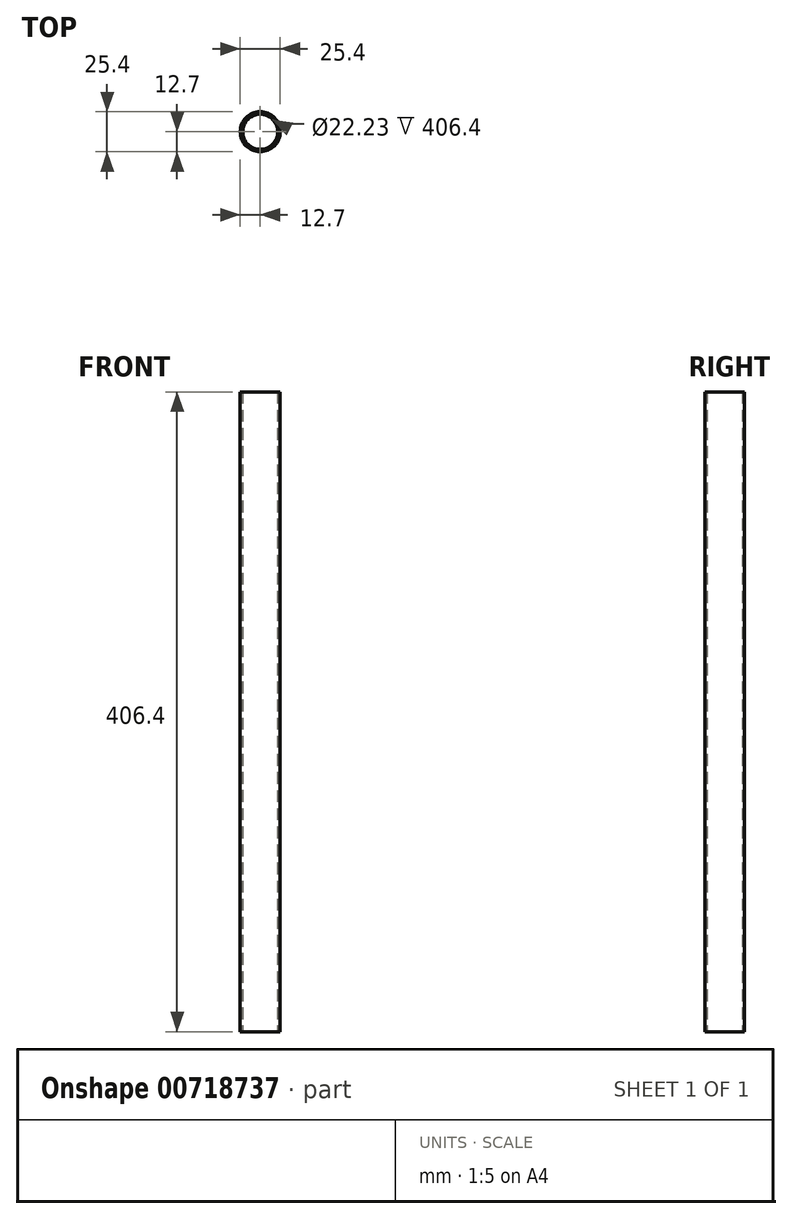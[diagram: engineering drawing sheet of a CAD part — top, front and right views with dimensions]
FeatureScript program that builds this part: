
annotation { "Feature Type Name" : "Feature", "Feature Type Description" : "" }
export const myFeature = defineFeature(function(context is Context, id is Id, definition is map)
    precondition{}
    {
        {
            var Q0;
            Q0=qCreatedBy(makeId("Top.planeOp"),FACE);
            var sketch = newSketch(context, id + "F0", { "sketchPlane" : qUnion([Q0])});
            skCircle(sketch, "E0", {"center": v(0, 0) * mm, "radius": 12.7 * mm});
            skCircle(sketch, "E1", {"center": v(0, 0) * mm, "radius": 11.11 * mm});
            skSolve(sketch);
        }
        {
            var Q0;
            Q0=makeQuery(id+"F0.imprint","IMPRINT",FACE,{"disambiguationData":[TD([[makeQuery(id+"F0.imprint","IMPRINT",EDGE,{"derivedFrom":sQuery(id+"F0.wireOp",EDGE,"E0")}),1.0]])]});
            extrude(context, id + "F1", {"entities" : qUnion([Q0]), "depth" : 406.4 * mm, "offsetDistance" : 25.4 * mm});
        }
    });
